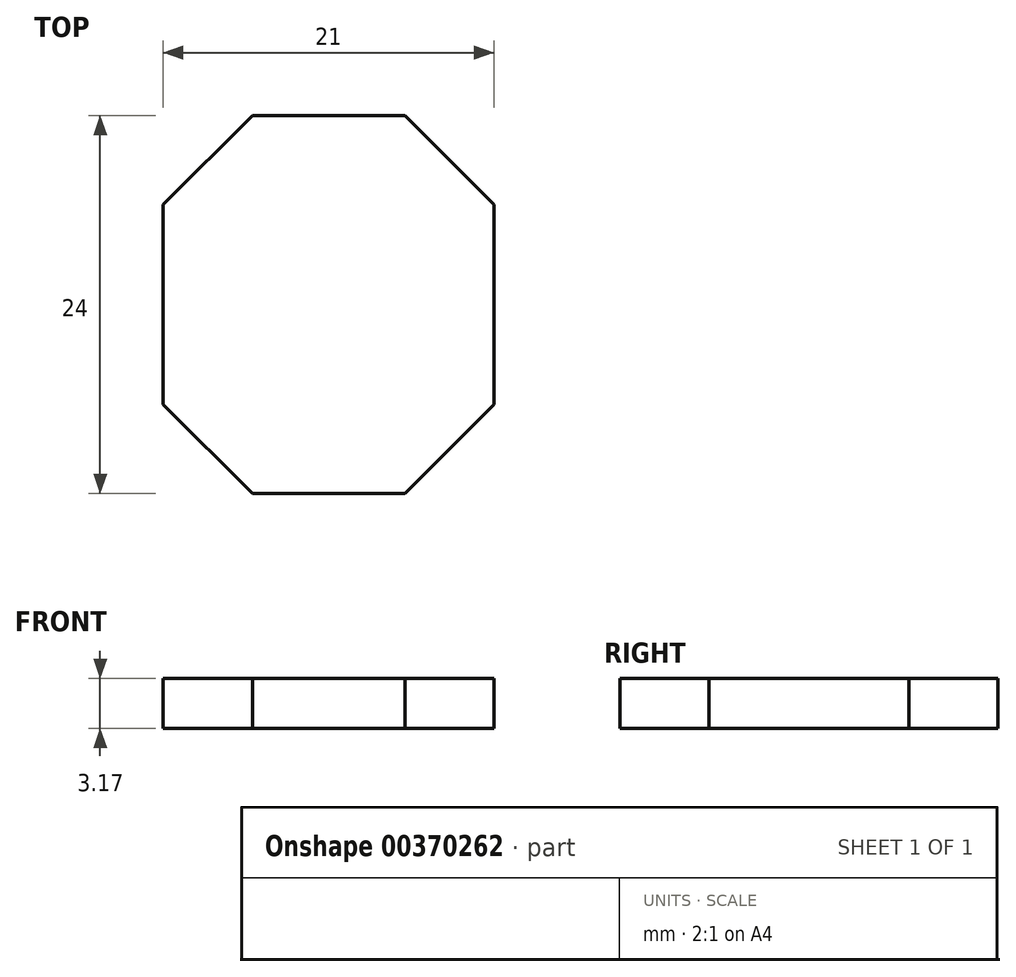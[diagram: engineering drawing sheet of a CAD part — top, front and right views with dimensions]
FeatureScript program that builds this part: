
annotation { "Feature Type Name" : "Feature", "Feature Type Description" : "" }
export const myFeature = defineFeature(function(context is Context, id is Id, definition is map)
    precondition{}
    {
        {
            var Q0;
            Q0=qCreatedBy(makeId("Top.planeOp"),FACE);
            var sketch = newSketch(context, id + "F0", { "sketchPlane" : qUnion([Q0])});
            skLineSegment(sketch, "E0.bottom", {"start": v(-3.7, 21.47) * mm, "end": v(-13.4, 21.47) * mm});
            skLineSegment(sketch, "E0.top", {"start": v(-3.7, -2.53) * mm, "end": v(-13.4, -2.53) * mm});
            skLineSegment(sketch, "E0.left", {"start": v(1.95, 15.82) * mm, "end": v(1.95, 3.13) * mm});
            skLineSegment(sketch, "E0.right", {"start": v(-19.05, 15.82) * mm, "end": v(-19.05, 3.13) * mm});
            skPoint(sketch, "E0.middle", {"position": v(-8.55, 9.47) * mm});
            skLineSegment(sketch, "E1", {"start": v(-13.4, 21.47) * mm, "end": v(-19.05, 15.82) * mm});
            skLineSegment(sketch, "E2", {"start": v(1.95, 3.13) * mm, "end": v(-3.7, -2.53) * mm});
            skLineSegment(sketch, "E3", {"start": v(-3.7, 21.47) * mm, "end": v(1.95, 15.82) * mm});
            skLineSegment(sketch, "E4", {"start": v(-19.05, 3.13) * mm, "end": v(-13.4, -2.53) * mm});
            skSolve(sketch);
        }
        {
            var Q0;
            Q0 = qSketchRegion(id + "F0", true);
            extrude(context, id + "F1", {"entities" : qUnion([Q0]), "depth" : 3.17 * mm});
        }
    });
